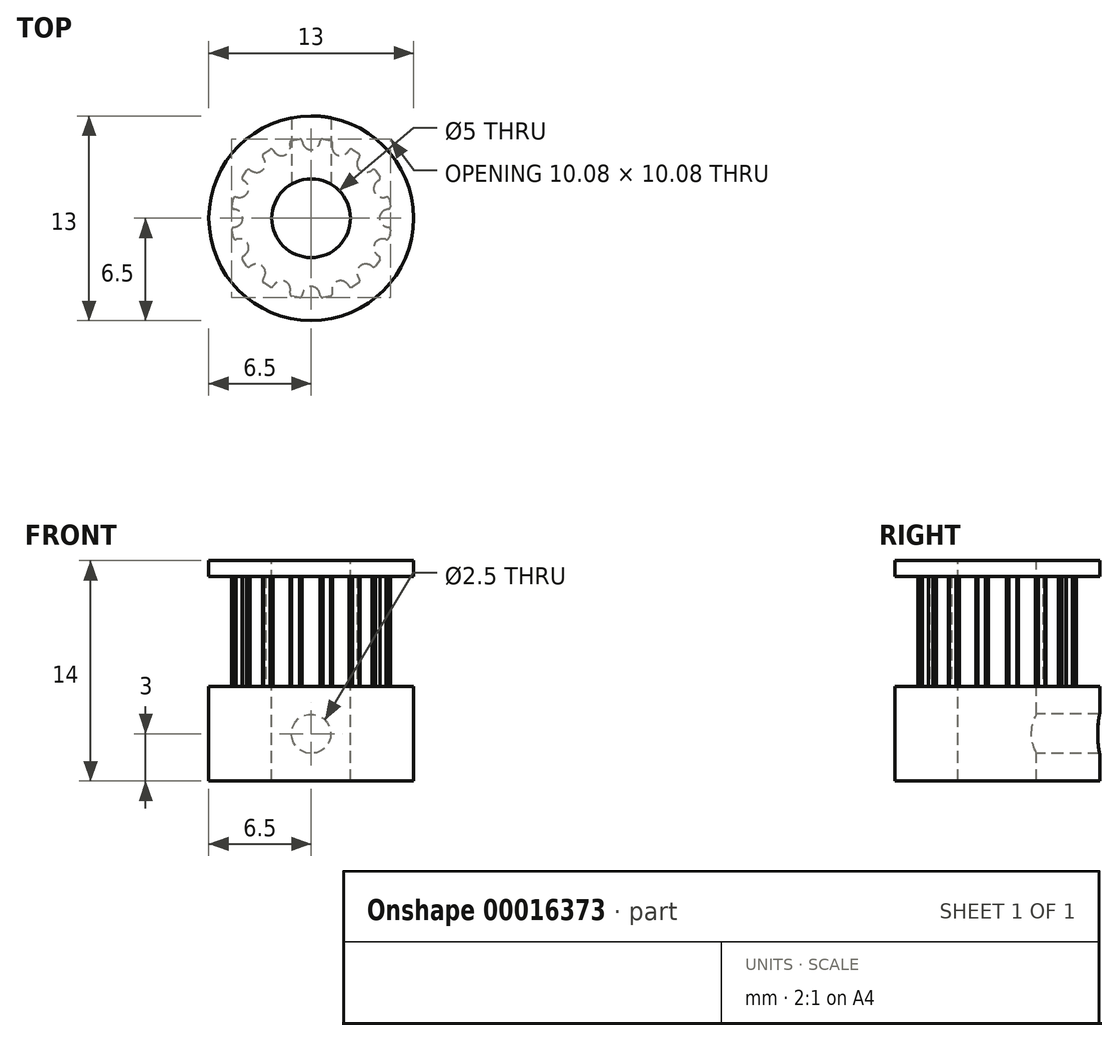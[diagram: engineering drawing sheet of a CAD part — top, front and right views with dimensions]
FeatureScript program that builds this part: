
annotation { "Feature Type Name" : "Feature", "Feature Type Description" : "" }
export const myFeature = defineFeature(function(context is Context, id is Id, definition is map)
    precondition{}
    {
        {
            var Q0;
            Q0=qCreatedBy(makeId("Top.planeOp"),FACE);
            var sketch = newSketch(context, id + "F0", { "sketchPlane" : qUnion([Q0])});
            skLineSegment(sketch, "E0", {"start": v(0, 0) * mm, "end": v(8.05, 0) * mm, "construction": true});
            skArc(sketch, "E1", {"start": v(5.1, 0) * mm, "mid": v(5, 1) * mm, "end": v(4.7, 1.95) * mm, "construction": true});
            skLineSegment(sketch, "E2", {"start": v(0, 0) * mm, "end": v(4.7, 1.95) * mm, "construction": true});
            skPoint(sketch, "E3", {"position": v(4.34, 0) * mm});
            skPoint(sketch, "E4", {"position": v(4.9, 0) * mm});
            skArc(sketch, "E5", {"start": v(4.68, 0.5) * mm, "mid": v(4.34, 0) * mm, "end": v(4.68, -0.5) * mm});
            skArc(sketch, "E6", {"start": v(4.9, 0.58) * mm, "mid": v(4.79, 0.55) * mm, "end": v(4.68, 0.5) * mm});
            skArc(sketch, "E7", {"start": v(4.94, 0) * mm, "mid": v(4.85, 0.96) * mm, "end": v(4.57, 1.9) * mm, "construction": true});
            skArc(sketch, "E8", {"start": v(4.9, 0.58) * mm, "mid": v(5, 0.64) * mm, "end": v(5.04, 0.75) * mm});
            skArc(sketch, "E9", {"start": v(4.97, -1.1) * mm, "mid": v(5.06, -0.56) * mm, "end": v(5.1, 0) * mm, "construction": true});
            skLineSegment(sketch, "E10", {"start": v(0, 0) * mm, "end": v(5, 1) * mm, "construction": true});
            skPoint(sketch, "E11", {"position": v(5, 1) * mm});
            skArc(sketch, "E12.MirrorCS", {"start": v(4.76, 1.34) * mm, "mid": v(4.87, 1.33) * mm, "end": v(4.94, 1.24) * mm});
            skArc(sketch, "E13.MirrorCS", {"start": v(4.76, 1.34) * mm, "mid": v(4.64, 1.32) * mm, "end": v(4.51, 1.32) * mm});
            skArc(sketch, "E14.MirrorCS", {"start": v(4.51, 1.32) * mm, "mid": v(4.01, 1.66) * mm, "end": v(4.12, 2.26) * mm});
            skLineSegment(sketch, "E15", {"start": v(4.94, 1.24) * mm, "end": v(5.04, 0.75) * mm});
            skArc(sketch, "E16.1.0", {"start": v(4.12, 2.26) * mm, "mid": v(4.01, 1.66) * mm, "end": v(4.51, 1.32) * mm});
            skArc(sketch, "E16.1.1", {"start": v(4.31, 2.41) * mm, "mid": v(4.21, 2.34) * mm, "end": v(4.12, 2.26) * mm});
            skArc(sketch, "E16.1.2", {"start": v(4.31, 2.41) * mm, "mid": v(4.38, 2.5) * mm, "end": v(4.37, 2.62) * mm});
            skLineSegment(sketch, "E16.1.3", {"start": v(4.1, 3.03) * mm, "end": v(4.37, 2.62) * mm});
            skArc(sketch, "E16.1.4", {"start": v(3.88, 3.06) * mm, "mid": v(4, 3.1) * mm, "end": v(4.1, 3.03) * mm});
            skArc(sketch, "E16.1.5", {"start": v(3.88, 3.06) * mm, "mid": v(3.78, 3) * mm, "end": v(3.67, 2.95) * mm});
            skArc(sketch, "E16.2.0", {"start": v(2.95, 3.67) * mm, "mid": v(3.07, 3.07) * mm, "end": v(3.67, 2.95) * mm});
            skArc(sketch, "E16.2.1", {"start": v(3.06, 3.88) * mm, "mid": v(3, 3.78) * mm, "end": v(2.95, 3.67) * mm});
            skArc(sketch, "E16.2.2", {"start": v(3.06, 3.88) * mm, "mid": v(3.1, 4) * mm, "end": v(3.03, 4.1) * mm});
            skLineSegment(sketch, "E16.2.3", {"start": v(2.62, 4.37) * mm, "end": v(3.03, 4.1) * mm});
            skArc(sketch, "E16.2.4", {"start": v(2.41, 4.31) * mm, "mid": v(2.5, 4.38) * mm, "end": v(2.62, 4.37) * mm});
            skArc(sketch, "E16.2.5", {"start": v(2.41, 4.31) * mm, "mid": v(2.34, 4.21) * mm, "end": v(2.26, 4.12) * mm});
            skArc(sketch, "E16.3.0", {"start": v(1.32, 4.51) * mm, "mid": v(1.66, 4.01) * mm, "end": v(2.26, 4.12) * mm});
            skArc(sketch, "E16.3.1", {"start": v(1.34, 4.76) * mm, "mid": v(1.32, 4.64) * mm, "end": v(1.32, 4.51) * mm});
            skArc(sketch, "E16.3.2", {"start": v(1.34, 4.76) * mm, "mid": v(1.33, 4.87) * mm, "end": v(1.24, 4.94) * mm});
            skLineSegment(sketch, "E16.3.3", {"start": v(0.75, 5.04) * mm, "end": v(1.24, 4.94) * mm});
            skArc(sketch, "E16.3.4", {"start": v(0.58, 4.9) * mm, "mid": v(0.64, 5) * mm, "end": v(0.75, 5.04) * mm});
            skArc(sketch, "E16.3.5", {"start": v(0.58, 4.9) * mm, "mid": v(0.55, 4.79) * mm, "end": v(0.5, 4.68) * mm});
            skArc(sketch, "E16.4.0", {"start": v(-0.5, 4.68) * mm, "mid": v(0, 4.34) * mm, "end": v(0.5, 4.68) * mm});
            skArc(sketch, "E16.4.1", {"start": v(-0.58, 4.9) * mm, "mid": v(-0.55, 4.79) * mm, "end": v(-0.5, 4.68) * mm});
            skArc(sketch, "E16.4.2", {"start": v(-0.58, 4.9) * mm, "mid": v(-0.64, 5) * mm, "end": v(-0.75, 5.04) * mm});
            skLineSegment(sketch, "E16.4.3", {"start": v(-1.24, 4.94) * mm, "end": v(-0.75, 5.04) * mm});
            skArc(sketch, "E16.4.4", {"start": v(-1.34, 4.76) * mm, "mid": v(-1.33, 4.87) * mm, "end": v(-1.24, 4.94) * mm});
            skArc(sketch, "E16.4.5", {"start": v(-1.34, 4.76) * mm, "mid": v(-1.32, 4.64) * mm, "end": v(-1.32, 4.51) * mm});
            skArc(sketch, "E16.5.0", {"start": v(-2.26, 4.12) * mm, "mid": v(-1.66, 4.01) * mm, "end": v(-1.32, 4.51) * mm});
            skArc(sketch, "E16.5.1", {"start": v(-2.41, 4.31) * mm, "mid": v(-2.34, 4.21) * mm, "end": v(-2.26, 4.12) * mm});
            skArc(sketch, "E16.5.2", {"start": v(-2.41, 4.31) * mm, "mid": v(-2.5, 4.38) * mm, "end": v(-2.62, 4.37) * mm});
            skLineSegment(sketch, "E16.5.3", {"start": v(-3.03, 4.1) * mm, "end": v(-2.62, 4.37) * mm});
            skArc(sketch, "E16.5.4", {"start": v(-3.06, 3.88) * mm, "mid": v(-3.1, 4) * mm, "end": v(-3.03, 4.1) * mm});
            skArc(sketch, "E16.5.5", {"start": v(-3.06, 3.88) * mm, "mid": v(-3, 3.78) * mm, "end": v(-2.95, 3.67) * mm});
            skArc(sketch, "E16.6.0", {"start": v(-3.67, 2.95) * mm, "mid": v(-3.07, 3.07) * mm, "end": v(-2.95, 3.67) * mm});
            skArc(sketch, "E16.6.1", {"start": v(-3.88, 3.06) * mm, "mid": v(-3.78, 3) * mm, "end": v(-3.67, 2.95) * mm});
            skArc(sketch, "E16.6.2", {"start": v(-3.88, 3.06) * mm, "mid": v(-4, 3.1) * mm, "end": v(-4.1, 3.03) * mm});
            skLineSegment(sketch, "E16.6.3", {"start": v(-4.37, 2.62) * mm, "end": v(-4.1, 3.03) * mm});
            skArc(sketch, "E16.6.4", {"start": v(-4.31, 2.41) * mm, "mid": v(-4.38, 2.5) * mm, "end": v(-4.37, 2.62) * mm});
            skArc(sketch, "E16.6.5", {"start": v(-4.31, 2.41) * mm, "mid": v(-4.21, 2.34) * mm, "end": v(-4.12, 2.26) * mm});
            skArc(sketch, "E16.7.0", {"start": v(-4.51, 1.32) * mm, "mid": v(-4.01, 1.66) * mm, "end": v(-4.12, 2.26) * mm});
            skArc(sketch, "E16.7.1", {"start": v(-4.76, 1.34) * mm, "mid": v(-4.64, 1.32) * mm, "end": v(-4.51, 1.32) * mm});
            skArc(sketch, "E16.7.2", {"start": v(-4.76, 1.34) * mm, "mid": v(-4.87, 1.33) * mm, "end": v(-4.94, 1.24) * mm});
            skLineSegment(sketch, "E16.7.3", {"start": v(-5.04, 0.75) * mm, "end": v(-4.94, 1.24) * mm});
            skArc(sketch, "E16.7.4", {"start": v(-4.9, 0.58) * mm, "mid": v(-5, 0.64) * mm, "end": v(-5.04, 0.75) * mm});
            skArc(sketch, "E16.7.5", {"start": v(-4.9, 0.58) * mm, "mid": v(-4.79, 0.55) * mm, "end": v(-4.68, 0.5) * mm});
            skArc(sketch, "E16.8.0", {"start": v(-4.68, -0.5) * mm, "mid": v(-4.34, 0) * mm, "end": v(-4.68, 0.5) * mm});
            skArc(sketch, "E16.8.1", {"start": v(-4.9, -0.58) * mm, "mid": v(-4.79, -0.55) * mm, "end": v(-4.68, -0.5) * mm});
            skArc(sketch, "E16.8.2", {"start": v(-4.9, -0.58) * mm, "mid": v(-5, -0.64) * mm, "end": v(-5.04, -0.75) * mm});
            skLineSegment(sketch, "E16.8.3", {"start": v(-4.94, -1.24) * mm, "end": v(-5.04, -0.75) * mm});
            skArc(sketch, "E16.8.4", {"start": v(-4.76, -1.34) * mm, "mid": v(-4.87, -1.33) * mm, "end": v(-4.94, -1.24) * mm});
            skArc(sketch, "E16.8.5", {"start": v(-4.76, -1.34) * mm, "mid": v(-4.64, -1.32) * mm, "end": v(-4.51, -1.32) * mm});
            skArc(sketch, "E16.9.0", {"start": v(-4.12, -2.26) * mm, "mid": v(-4.01, -1.66) * mm, "end": v(-4.51, -1.32) * mm});
            skArc(sketch, "E16.9.1", {"start": v(-4.31, -2.41) * mm, "mid": v(-4.21, -2.34) * mm, "end": v(-4.12, -2.26) * mm});
            skArc(sketch, "E16.9.2", {"start": v(-4.31, -2.41) * mm, "mid": v(-4.38, -2.5) * mm, "end": v(-4.37, -2.62) * mm});
            skLineSegment(sketch, "E16.9.3", {"start": v(-4.1, -3.03) * mm, "end": v(-4.37, -2.62) * mm});
            skArc(sketch, "E16.9.4", {"start": v(-3.88, -3.06) * mm, "mid": v(-4, -3.1) * mm, "end": v(-4.1, -3.03) * mm});
            skArc(sketch, "E16.9.5", {"start": v(-3.88, -3.06) * mm, "mid": v(-3.78, -3) * mm, "end": v(-3.67, -2.95) * mm});
            skArc(sketch, "E16.10.0", {"start": v(-2.95, -3.67) * mm, "mid": v(-3.07, -3.07) * mm, "end": v(-3.67, -2.95) * mm});
            skArc(sketch, "E16.10.1", {"start": v(-3.06, -3.88) * mm, "mid": v(-3, -3.78) * mm, "end": v(-2.95, -3.67) * mm});
            skArc(sketch, "E16.10.2", {"start": v(-3.06, -3.88) * mm, "mid": v(-3.1, -4) * mm, "end": v(-3.03, -4.1) * mm});
            skLineSegment(sketch, "E16.10.3", {"start": v(-2.62, -4.37) * mm, "end": v(-3.03, -4.1) * mm});
            skArc(sketch, "E16.10.4", {"start": v(-2.41, -4.31) * mm, "mid": v(-2.5, -4.38) * mm, "end": v(-2.62, -4.37) * mm});
            skArc(sketch, "E16.10.5", {"start": v(-2.41, -4.31) * mm, "mid": v(-2.34, -4.21) * mm, "end": v(-2.26, -4.12) * mm});
            skArc(sketch, "E16.11.0", {"start": v(-1.32, -4.51) * mm, "mid": v(-1.66, -4.01) * mm, "end": v(-2.26, -4.12) * mm});
            skArc(sketch, "E16.11.1", {"start": v(-1.34, -4.76) * mm, "mid": v(-1.32, -4.64) * mm, "end": v(-1.32, -4.51) * mm});
            skArc(sketch, "E16.11.2", {"start": v(-1.34, -4.76) * mm, "mid": v(-1.33, -4.87) * mm, "end": v(-1.24, -4.94) * mm});
            skLineSegment(sketch, "E16.11.3", {"start": v(-0.75, -5.04) * mm, "end": v(-1.24, -4.94) * mm});
            skArc(sketch, "E16.11.4", {"start": v(-0.58, -4.9) * mm, "mid": v(-0.64, -5) * mm, "end": v(-0.75, -5.04) * mm});
            skArc(sketch, "E16.11.5", {"start": v(-0.58, -4.9) * mm, "mid": v(-0.55, -4.79) * mm, "end": v(-0.5, -4.68) * mm});
            skArc(sketch, "E16.12.0", {"start": v(0.5, -4.68) * mm, "mid": v(0, -4.34) * mm, "end": v(-0.5, -4.68) * mm});
            skArc(sketch, "E16.12.1", {"start": v(0.58, -4.9) * mm, "mid": v(0.55, -4.79) * mm, "end": v(0.5, -4.68) * mm});
            skArc(sketch, "E16.12.2", {"start": v(0.58, -4.9) * mm, "mid": v(0.64, -5) * mm, "end": v(0.75, -5.04) * mm});
            skLineSegment(sketch, "E16.12.3", {"start": v(1.24, -4.94) * mm, "end": v(0.75, -5.04) * mm});
            skArc(sketch, "E16.12.4", {"start": v(1.34, -4.76) * mm, "mid": v(1.33, -4.87) * mm, "end": v(1.24, -4.94) * mm});
            skArc(sketch, "E16.12.5", {"start": v(1.34, -4.76) * mm, "mid": v(1.32, -4.64) * mm, "end": v(1.32, -4.51) * mm});
            skArc(sketch, "E16.13.0", {"start": v(2.26, -4.12) * mm, "mid": v(1.66, -4.01) * mm, "end": v(1.32, -4.51) * mm});
            skArc(sketch, "E16.13.1", {"start": v(2.41, -4.31) * mm, "mid": v(2.34, -4.21) * mm, "end": v(2.26, -4.12) * mm});
            skArc(sketch, "E16.13.2", {"start": v(2.41, -4.31) * mm, "mid": v(2.5, -4.38) * mm, "end": v(2.62, -4.37) * mm});
            skLineSegment(sketch, "E16.13.3", {"start": v(3.03, -4.1) * mm, "end": v(2.62, -4.37) * mm});
            skArc(sketch, "E16.13.4", {"start": v(3.06, -3.88) * mm, "mid": v(3.1, -4) * mm, "end": v(3.03, -4.1) * mm});
            skArc(sketch, "E16.13.5", {"start": v(3.06, -3.88) * mm, "mid": v(3, -3.78) * mm, "end": v(2.95, -3.67) * mm});
            skArc(sketch, "E16.14.0", {"start": v(3.67, -2.95) * mm, "mid": v(3.07, -3.07) * mm, "end": v(2.95, -3.67) * mm});
            skArc(sketch, "E16.14.1", {"start": v(3.88, -3.06) * mm, "mid": v(3.78, -3) * mm, "end": v(3.67, -2.95) * mm});
            skArc(sketch, "E16.14.2", {"start": v(3.88, -3.06) * mm, "mid": v(4, -3.1) * mm, "end": v(4.1, -3.03) * mm});
            skLineSegment(sketch, "E16.14.3", {"start": v(4.37, -2.62) * mm, "end": v(4.1, -3.03) * mm});
            skArc(sketch, "E16.14.4", {"start": v(4.31, -2.41) * mm, "mid": v(4.38, -2.5) * mm, "end": v(4.37, -2.62) * mm});
            skArc(sketch, "E16.14.5", {"start": v(4.31, -2.41) * mm, "mid": v(4.21, -2.34) * mm, "end": v(4.12, -2.26) * mm});
            skArc(sketch, "E16.15.0", {"start": v(4.51, -1.32) * mm, "mid": v(4.01, -1.66) * mm, "end": v(4.12, -2.26) * mm});
            skArc(sketch, "E16.15.1", {"start": v(4.76, -1.34) * mm, "mid": v(4.64, -1.32) * mm, "end": v(4.51, -1.32) * mm});
            skArc(sketch, "E16.15.2", {"start": v(4.76, -1.34) * mm, "mid": v(4.87, -1.33) * mm, "end": v(4.94, -1.24) * mm});
            skLineSegment(sketch, "E16.15.3", {"start": v(5.04, -0.75) * mm, "end": v(4.94, -1.24) * mm});
            skArc(sketch, "E16.15.4", {"start": v(4.9, -0.58) * mm, "mid": v(5, -0.64) * mm, "end": v(5.04, -0.75) * mm});
            skArc(sketch, "E16.15.5", {"start": v(4.9, -0.58) * mm, "mid": v(4.79, -0.55) * mm, "end": v(4.68, -0.5) * mm});
            skCircle(sketch, "E17", {"center": v(0, 0) * mm, "radius": 2.5 * mm});
            skCircle(sketch, "E18", {"center": v(0, 0) * mm, "radius": 6.5 * mm});
            skSolve(sketch);
        }
        {
            var Q0;
            Q0=makeQuery(id+"F0.imprint","IMPRINT",FACE,{"disambiguationData":[TD([[makeQuery(id+"F0.imprint","IMPRINT",EDGE,{"derivedFrom":sQuery(id+"F0.wireOp",EDGE,"E5")}),-1.0]])]});
            var Q1;
            Q1=makeQuery(id+"F0.imprint","IMPRINT",FACE,{"disambiguationData":[TD([[makeQuery(id+"F0.imprint","IMPRINT",EDGE,{"derivedFrom":sQuery(id+"F0.wireOp",EDGE,"E5")}),1.0]])]});
            extrude(context, id + "F1", {"entities" : qUnion([Q0, Q1]), "oppositeDirection" : true, "depth" : 6 * mm});
        }
        {
            var Q0;
            Q0=makeQuery(id+"F0.imprint","IMPRINT",FACE,{"disambiguationData":[TD([[makeQuery(id+"F0.imprint","IMPRINT",EDGE,{"derivedFrom":sQuery(id+"F0.wireOp",EDGE,"E5")}),-1.0]])]});
            extrude(context, id + "F2", {"entities" : qUnion([Q0]), "operationType" : NewBodyOperationType.ADD, "depth" : 7 * mm});
        }
        {
            var Q0;
            Q0=makeQuery(id+"F0.imprint","IMPRINT",FACE,{"disambiguationData":[TD([[makeQuery(id+"F0.imprint","IMPRINT",EDGE,{"derivedFrom":sQuery(id+"F0.wireOp",EDGE,"E5")}),1.0]])]});
            var Q1;
            Q1=makeQuery(id+"F0.imprint","IMPRINT",FACE,{"disambiguationData":[TD([[makeQuery(id+"F0.imprint","IMPRINT",EDGE,{"derivedFrom":sQuery(id+"F0.wireOp",EDGE,"E5")}),-1.0]])]});
            var Q2;
            Q2=makeQuery(id+"F2.opExtrude","CAP_FACE",FACE,{"disambiguationData":[OSD([sQuery(id+"F0.wireOp",EDGE,"E5"),sQuery(id+"F0.wireOp",EDGE,"E6"),sQuery(id+"F0.wireOp",EDGE,"E8"),sQuery(id+"F0.wireOp",EDGE,"E12.MirrorCS"),sQuery(id+"F0.wireOp",EDGE,"E13.MirrorCS"),sQuery(id+"F0.wireOp",EDGE,"E15"),sQuery(id+"F0.wireOp",EDGE,"E16.1.0"),sQuery(id+"F0.wireOp",EDGE,"E16.1.1"),sQuery(id+"F0.wireOp",EDGE,"E16.1.2"),sQuery(id+"F0.wireOp",EDGE,"E16.1.3"),sQuery(id+"F0.wireOp",EDGE,"E16.1.4"),sQuery(id+"F0.wireOp",EDGE,"E16.1.5"),sQuery(id+"F0.wireOp",EDGE,"E16.2.0"),sQuery(id+"F0.wireOp",EDGE,"E16.2.1"),sQuery(id+"F0.wireOp",EDGE,"E16.2.2"),sQuery(id+"F0.wireOp",EDGE,"E16.2.3"),sQuery(id+"F0.wireOp",EDGE,"E16.2.4"),sQuery(id+"F0.wireOp",EDGE,"E16.2.5"),sQuery(id+"F0.wireOp",EDGE,"E16.3.0"),sQuery(id+"F0.wireOp",EDGE,"E16.3.1"),sQuery(id+"F0.wireOp",EDGE,"E16.3.2"),sQuery(id+"F0.wireOp",EDGE,"E16.3.3"),sQuery(id+"F0.wireOp",EDGE,"E16.3.4"),sQuery(id+"F0.wireOp",EDGE,"E16.3.5"),sQuery(id+"F0.wireOp",EDGE,"E16.4.0"),sQuery(id+"F0.wireOp",EDGE,"E16.4.1"),sQuery(id+"F0.wireOp",EDGE,"E16.4.2"),sQuery(id+"F0.wireOp",EDGE,"E16.4.3"),sQuery(id+"F0.wireOp",EDGE,"E16.4.4"),sQuery(id+"F0.wireOp",EDGE,"E16.4.5"),sQuery(id+"F0.wireOp",EDGE,"E16.5.0"),sQuery(id+"F0.wireOp",EDGE,"E16.5.1"),sQuery(id+"F0.wireOp",EDGE,"E16.5.2"),sQuery(id+"F0.wireOp",EDGE,"E16.5.3"),sQuery(id+"F0.wireOp",EDGE,"E16.5.4"),sQuery(id+"F0.wireOp",EDGE,"E16.5.5"),sQuery(id+"F0.wireOp",EDGE,"E16.6.0"),sQuery(id+"F0.wireOp",EDGE,"E16.6.1"),sQuery(id+"F0.wireOp",EDGE,"E16.6.2"),sQuery(id+"F0.wireOp",EDGE,"E16.6.3"),sQuery(id+"F0.wireOp",EDGE,"E16.6.4"),sQuery(id+"F0.wireOp",EDGE,"E16.6.5"),sQuery(id+"F0.wireOp",EDGE,"E16.7.0"),sQuery(id+"F0.wireOp",EDGE,"E16.7.1"),sQuery(id+"F0.wireOp",EDGE,"E16.7.2"),sQuery(id+"F0.wireOp",EDGE,"E16.7.3"),sQuery(id+"F0.wireOp",EDGE,"E16.7.4"),sQuery(id+"F0.wireOp",EDGE,"E16.7.5"),sQuery(id+"F0.wireOp",EDGE,"E16.8.0"),sQuery(id+"F0.wireOp",EDGE,"E16.8.1"),sQuery(id+"F0.wireOp",EDGE,"E16.8.2"),sQuery(id+"F0.wireOp",EDGE,"E16.8.3"),sQuery(id+"F0.wireOp",EDGE,"E16.8.4"),sQuery(id+"F0.wireOp",EDGE,"E16.8.5"),sQuery(id+"F0.wireOp",EDGE,"E16.9.0"),sQuery(id+"F0.wireOp",EDGE,"E16.9.1"),sQuery(id+"F0.wireOp",EDGE,"E16.9.2"),sQuery(id+"F0.wireOp",EDGE,"E16.9.3"),sQuery(id+"F0.wireOp",EDGE,"E16.9.4"),sQuery(id+"F0.wireOp",EDGE,"E16.9.5"),sQuery(id+"F0.wireOp",EDGE,"E16.10.0"),sQuery(id+"F0.wireOp",EDGE,"E16.10.1"),sQuery(id+"F0.wireOp",EDGE,"E16.10.2"),sQuery(id+"F0.wireOp",EDGE,"E16.10.3"),sQuery(id+"F0.wireOp",EDGE,"E16.10.4"),sQuery(id+"F0.wireOp",EDGE,"E16.10.5"),sQuery(id+"F0.wireOp",EDGE,"E16.11.0"),sQuery(id+"F0.wireOp",EDGE,"E16.11.1"),sQuery(id+"F0.wireOp",EDGE,"E16.11.2"),sQuery(id+"F0.wireOp",EDGE,"E16.11.3"),sQuery(id+"F0.wireOp",EDGE,"E16.11.4"),sQuery(id+"F0.wireOp",EDGE,"E16.11.5"),sQuery(id+"F0.wireOp",EDGE,"E16.12.0"),sQuery(id+"F0.wireOp",EDGE,"E16.12.1"),sQuery(id+"F0.wireOp",EDGE,"E16.12.2"),sQuery(id+"F0.wireOp",EDGE,"E16.12.3"),sQuery(id+"F0.wireOp",EDGE,"E16.12.4"),sQuery(id+"F0.wireOp",EDGE,"E16.12.5"),sQuery(id+"F0.wireOp",EDGE,"E16.13.0"),sQuery(id+"F0.wireOp",EDGE,"E16.13.1"),sQuery(id+"F0.wireOp",EDGE,"E16.13.2"),sQuery(id+"F0.wireOp",EDGE,"E16.13.3"),sQuery(id+"F0.wireOp",EDGE,"E16.13.4"),sQuery(id+"F0.wireOp",EDGE,"E16.13.5"),sQuery(id+"F0.wireOp",EDGE,"E16.14.0"),sQuery(id+"F0.wireOp",EDGE,"E16.14.1"),sQuery(id+"F0.wireOp",EDGE,"E16.14.2"),sQuery(id+"F0.wireOp",EDGE,"E16.14.3"),sQuery(id+"F0.wireOp",EDGE,"E16.14.4"),sQuery(id+"F0.wireOp",EDGE,"E16.14.5"),sQuery(id+"F0.wireOp",EDGE,"E16.15.0"),sQuery(id+"F0.wireOp",EDGE,"E16.15.1"),sQuery(id+"F0.wireOp",EDGE,"E16.15.2"),sQuery(id+"F0.wireOp",EDGE,"E16.15.3"),sQuery(id+"F0.wireOp",EDGE,"E16.15.4"),sQuery(id+"F0.wireOp",EDGE,"E16.15.5"),sQuery(id+"F0.wireOp",EDGE,"E17")])],"isStart":false});
            var Q3;
            Q3=makeQuery(id+"F2.opExtrude","CAP_FACE",FACE,{"disambiguationData":[OSD([sQuery(id+"F0.wireOp",EDGE,"E5"),sQuery(id+"F0.wireOp",EDGE,"E6"),sQuery(id+"F0.wireOp",EDGE,"E8"),sQuery(id+"F0.wireOp",EDGE,"E12.MirrorCS"),sQuery(id+"F0.wireOp",EDGE,"E13.MirrorCS"),sQuery(id+"F0.wireOp",EDGE,"E15"),sQuery(id+"F0.wireOp",EDGE,"E16.1.0"),sQuery(id+"F0.wireOp",EDGE,"E16.1.1"),sQuery(id+"F0.wireOp",EDGE,"E16.1.2"),sQuery(id+"F0.wireOp",EDGE,"E16.1.3"),sQuery(id+"F0.wireOp",EDGE,"E16.1.4"),sQuery(id+"F0.wireOp",EDGE,"E16.1.5"),sQuery(id+"F0.wireOp",EDGE,"E16.2.0"),sQuery(id+"F0.wireOp",EDGE,"E16.2.1"),sQuery(id+"F0.wireOp",EDGE,"E16.2.2"),sQuery(id+"F0.wireOp",EDGE,"E16.2.3"),sQuery(id+"F0.wireOp",EDGE,"E16.2.4"),sQuery(id+"F0.wireOp",EDGE,"E16.2.5"),sQuery(id+"F0.wireOp",EDGE,"E16.3.0"),sQuery(id+"F0.wireOp",EDGE,"E16.3.1"),sQuery(id+"F0.wireOp",EDGE,"E16.3.2"),sQuery(id+"F0.wireOp",EDGE,"E16.3.3"),sQuery(id+"F0.wireOp",EDGE,"E16.3.4"),sQuery(id+"F0.wireOp",EDGE,"E16.3.5"),sQuery(id+"F0.wireOp",EDGE,"E16.4.0"),sQuery(id+"F0.wireOp",EDGE,"E16.4.1"),sQuery(id+"F0.wireOp",EDGE,"E16.4.2"),sQuery(id+"F0.wireOp",EDGE,"E16.4.3"),sQuery(id+"F0.wireOp",EDGE,"E16.4.4"),sQuery(id+"F0.wireOp",EDGE,"E16.4.5"),sQuery(id+"F0.wireOp",EDGE,"E16.5.0"),sQuery(id+"F0.wireOp",EDGE,"E16.5.1"),sQuery(id+"F0.wireOp",EDGE,"E16.5.2"),sQuery(id+"F0.wireOp",EDGE,"E16.5.3"),sQuery(id+"F0.wireOp",EDGE,"E16.5.4"),sQuery(id+"F0.wireOp",EDGE,"E16.5.5"),sQuery(id+"F0.wireOp",EDGE,"E16.6.0"),sQuery(id+"F0.wireOp",EDGE,"E16.6.1"),sQuery(id+"F0.wireOp",EDGE,"E16.6.2"),sQuery(id+"F0.wireOp",EDGE,"E16.6.3"),sQuery(id+"F0.wireOp",EDGE,"E16.6.4"),sQuery(id+"F0.wireOp",EDGE,"E16.6.5"),sQuery(id+"F0.wireOp",EDGE,"E16.7.0"),sQuery(id+"F0.wireOp",EDGE,"E16.7.1"),sQuery(id+"F0.wireOp",EDGE,"E16.7.2"),sQuery(id+"F0.wireOp",EDGE,"E16.7.3"),sQuery(id+"F0.wireOp",EDGE,"E16.7.4"),sQuery(id+"F0.wireOp",EDGE,"E16.7.5"),sQuery(id+"F0.wireOp",EDGE,"E16.8.0"),sQuery(id+"F0.wireOp",EDGE,"E16.8.1"),sQuery(id+"F0.wireOp",EDGE,"E16.8.2"),sQuery(id+"F0.wireOp",EDGE,"E16.8.3"),sQuery(id+"F0.wireOp",EDGE,"E16.8.4"),sQuery(id+"F0.wireOp",EDGE,"E16.8.5"),sQuery(id+"F0.wireOp",EDGE,"E16.9.0"),sQuery(id+"F0.wireOp",EDGE,"E16.9.1"),sQuery(id+"F0.wireOp",EDGE,"E16.9.2"),sQuery(id+"F0.wireOp",EDGE,"E16.9.3"),sQuery(id+"F0.wireOp",EDGE,"E16.9.4"),sQuery(id+"F0.wireOp",EDGE,"E16.9.5"),sQuery(id+"F0.wireOp",EDGE,"E16.10.0"),sQuery(id+"F0.wireOp",EDGE,"E16.10.1"),sQuery(id+"F0.wireOp",EDGE,"E16.10.2"),sQuery(id+"F0.wireOp",EDGE,"E16.10.3"),sQuery(id+"F0.wireOp",EDGE,"E16.10.4"),sQuery(id+"F0.wireOp",EDGE,"E16.10.5"),sQuery(id+"F0.wireOp",EDGE,"E16.11.0"),sQuery(id+"F0.wireOp",EDGE,"E16.11.1"),sQuery(id+"F0.wireOp",EDGE,"E16.11.2"),sQuery(id+"F0.wireOp",EDGE,"E16.11.3"),sQuery(id+"F0.wireOp",EDGE,"E16.11.4"),sQuery(id+"F0.wireOp",EDGE,"E16.11.5"),sQuery(id+"F0.wireOp",EDGE,"E16.12.0"),sQuery(id+"F0.wireOp",EDGE,"E16.12.1"),sQuery(id+"F0.wireOp",EDGE,"E16.12.2"),sQuery(id+"F0.wireOp",EDGE,"E16.12.3"),sQuery(id+"F0.wireOp",EDGE,"E16.12.4"),sQuery(id+"F0.wireOp",EDGE,"E16.12.5"),sQuery(id+"F0.wireOp",EDGE,"E16.13.0"),sQuery(id+"F0.wireOp",EDGE,"E16.13.1"),sQuery(id+"F0.wireOp",EDGE,"E16.13.2"),sQuery(id+"F0.wireOp",EDGE,"E16.13.3"),sQuery(id+"F0.wireOp",EDGE,"E16.13.4"),sQuery(id+"F0.wireOp",EDGE,"E16.13.5"),sQuery(id+"F0.wireOp",EDGE,"E16.14.0"),sQuery(id+"F0.wireOp",EDGE,"E16.14.1"),sQuery(id+"F0.wireOp",EDGE,"E16.14.2"),sQuery(id+"F0.wireOp",EDGE,"E16.14.3"),sQuery(id+"F0.wireOp",EDGE,"E16.14.4"),sQuery(id+"F0.wireOp",EDGE,"E16.14.5"),sQuery(id+"F0.wireOp",EDGE,"E16.15.0"),sQuery(id+"F0.wireOp",EDGE,"E16.15.1"),sQuery(id+"F0.wireOp",EDGE,"E16.15.2"),sQuery(id+"F0.wireOp",EDGE,"E16.15.3"),sQuery(id+"F0.wireOp",EDGE,"E16.15.4"),sQuery(id+"F0.wireOp",EDGE,"E16.15.5"),sQuery(id+"F0.wireOp",EDGE,"E17")])],"isStart":false});
            extrude(context, id + "F3", {"entities" : qUnion([Q0, Q1]), "operationType" : NewBodyOperationType.ADD, "endBoundEntityFace" : qUnion([Q2]), "depth" : 8 * mm, "hasSecondDirection" : true, "secondDirectionBound" : SecondDirectionBoundingType.UP_TO_SURFACE, "secondDirectionOppositeDirection" : false, "secondDirectionBoundEntityFace" : qUnion([Q3]), "secondDirectionDepth" : 8 * mm});
        }
        {
            var Q0;
            Q0=qCreatedBy(makeId("Front.planeOp"),FACE);
            var sketch = newSketch(context, id + "F4", { "sketchPlane" : qUnion([Q0])});
            skLineSegment(sketch, "E19", {"start": v(0, 0) * mm, "end": v(-6.5, 0) * mm, "construction": true});
            skLineSegment(sketch, "E20", {"start": v(-6.5, 0) * mm, "end": v(-6.5, -6) * mm, "construction": true});
            skLineSegment(sketch, "E21", {"start": v(-6.5, -6) * mm, "end": v(6.5, -6) * mm, "construction": true});
            skLineSegment(sketch, "E22", {"start": v(6.5, -6) * mm, "end": v(6.5, 0) * mm, "construction": true});
            skLineSegment(sketch, "E23", {"start": v(6.5, 0) * mm, "end": v(0, 0) * mm, "construction": true});
            skPoint(sketch, "E24", {"position": v(-6.5, -3) * mm});
            skPoint(sketch, "E25", {"position": v(0, -3) * mm});
            skCircle(sketch, "E26", {"center": v(0, -3) * mm, "radius": 1.25 * mm});
            skSolve(sketch);
        }
        {
            var Q0;
            Q0=qSketchRegion(id+"F4",true);
            extrude(context, id + "F5", {"entities" : qUnion([Q0]), "operationType" : NewBodyOperationType.REMOVE, "oppositeDirection" : true, "depth" : 25 * mm});
        }
    });
